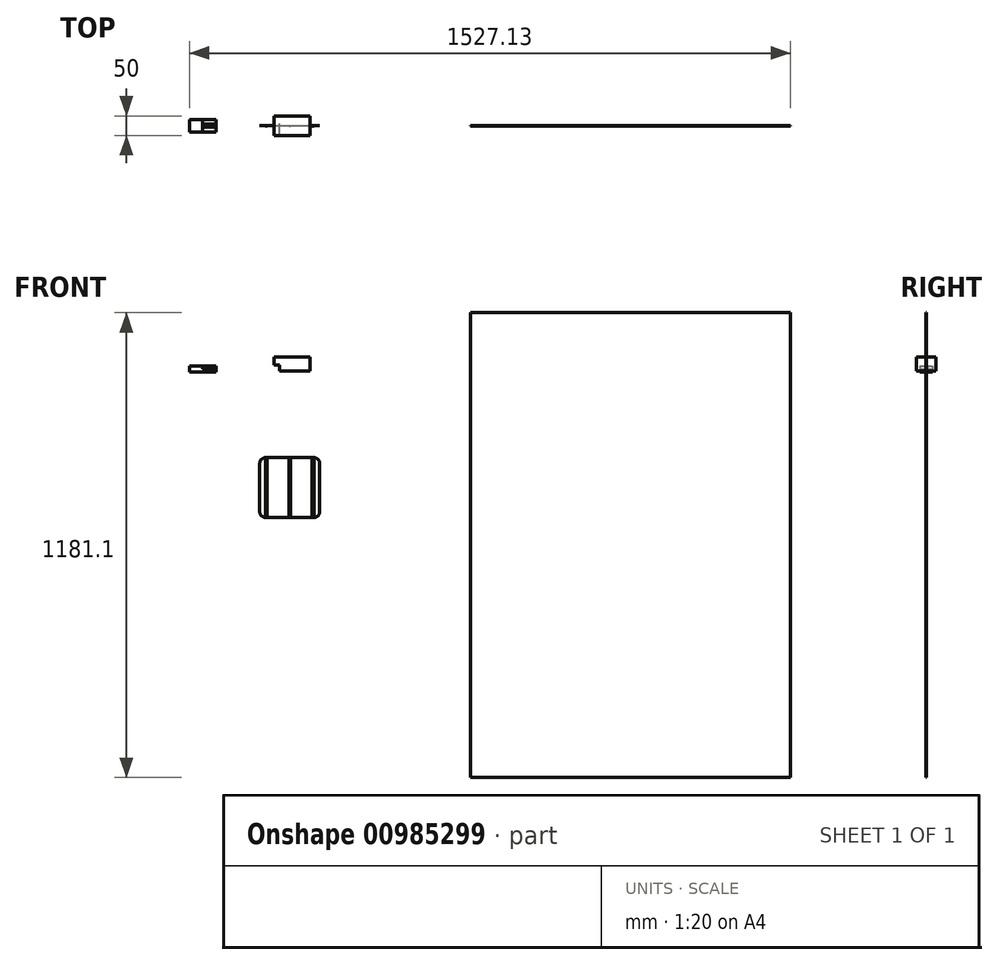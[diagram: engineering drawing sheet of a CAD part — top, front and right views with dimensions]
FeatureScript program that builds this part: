
annotation { "Feature Type Name" : "Feature", "Feature Type Description" : "" }
export const myFeature = defineFeature(function(context is Context, id is Id, definition is map)
    precondition{}
    {
        {
            var Q0;
            Q0=qCreatedBy(makeId("Front.planeOp"),FACE);
            var sketch = newSketch(context, id + "F0", { "sketchPlane" : qUnion([Q0])});
            skLineSegment(sketch, "E0", {"start": v(1286.74, 1046.2) * mm, "end": v(2099.54, 1046.2) * mm});
            skLineSegment(sketch, "E1", {"start": v(2099.54, -134.9) * mm, "end": v(1286.74, -134.9) * mm});
            skLineSegment(sketch, "E2", {"start": v(1286.74, 1046.2) * mm, "end": v(1286.74, -134.9) * mm});
            skLineSegment(sketch, "E3", {"start": v(2099.54, 1046.2) * mm, "end": v(2099.54, -134.9) * mm});
            skSolve(sketch);
        }
        {
            var Q0;
            Q0=makeQuery(id+"F0.imprint","IMPRINT",FACE,{"disambiguationData":[TD([[makeQuery(id+"F0.imprint","IMPRINT",EDGE,{"derivedFrom":sQuery(id+"F0.wireOp",EDGE,"E0")}),-1.0]])]});
            var sketch = newSketch(context, id + "F1", { "sketchPlane" : qUnion([Q0])});
            skLineSegment(sketch, "E4.bottom", {"start": v(766.3, 678.17) * mm, "end": v(888.7, 678.17) * mm});
            skLineSegment(sketch, "E4.top", {"start": v(766.3, 525.77) * mm, "end": v(888.7, 525.77) * mm});
            skLineSegment(sketch, "E4.left", {"start": v(751.3, 663.17) * mm, "end": v(751.3, 540.77) * mm});
            skLineSegment(sketch, "E4.right", {"start": v(903.7, 663.17) * mm, "end": v(903.7, 540.77) * mm});
            skPoint(sketch, "E5.visualSharp", {"position": v(751.3, 678.17) * mm});
            skArc(sketch, "E5.filletArc", {"start": v(766.3, 678.17) * mm, "mid": v(755.7, 673.78) * mm, "end": v(751.3, 663.17) * mm});
            skPoint(sketch, "E6.visualSharp", {"position": v(903.7, 678.17) * mm});
            skArc(sketch, "E6.filletArc", {"start": v(903.7, 663.17) * mm, "mid": v(899.3, 673.78) * mm, "end": v(888.7, 678.17) * mm});
            skPoint(sketch, "E7.visualSharp", {"position": v(903.7, 525.77) * mm});
            skArc(sketch, "E7.filletArc", {"start": v(888.7, 525.77) * mm, "mid": v(899.3, 530.16) * mm, "end": v(903.7, 540.77) * mm});
            skPoint(sketch, "E8.visualSharp", {"position": v(751.3, 525.77) * mm});
            skArc(sketch, "E8.filletArc", {"start": v(751.3, 540.77) * mm, "mid": v(755.7, 530.16) * mm, "end": v(766.3, 525.77) * mm});
            skLineSegment(sketch, "E9.bottom", {"start": v(3038.85, 81858.35) * mm, "end": v(2869.38, 81858.35) * mm});
            skLineSegment(sketch, "E9.top", {"start": v(3038.85, 72650.5) * mm, "end": v(2869.38, 72650.5) * mm});
            skLineSegment(sketch, "E9.left", {"start": v(3038.85, 81858.35) * mm, "end": v(3038.85, 72650.5) * mm});
            skLineSegment(sketch, "E9.right", {"start": v(2869.38, 81858.35) * mm, "end": v(2869.38, 72650.5) * mm});
            skSolve(sketch);
        }
        {
            var Q0;
            Q0=makeQuery(id+"F0.imprint","IMPRINT",FACE,{"disambiguationData":[TD([[makeQuery(id+"F0.imprint","IMPRINT",EDGE,{"derivedFrom":sQuery(id+"F0.wireOp",EDGE,"E0")}),-1.0]])]});
            extrude(context, id + "F2", {"entities" : qUnion([Q0]), "depth" : 1 * mm, "offsetDistance" : 25 * mm});
        }
        {
            var Q0;
            Q0=makeQuery(id+"F1.imprint","IMPRINT",FACE,{"disambiguationData":[TD([[makeQuery(id+"F1.imprint","IMPRINT",EDGE,{"derivedFrom":sQuery(id+"F1.wireOp",EDGE,"E4.bottom")}),-1.0]])]});
            extrude(context, id + "F3", {"entities" : qUnion([Q0]), "depth" : 1 * mm, "offsetDistance" : 25 * mm});
        }
        {
            var Q0;
            Q0=makeQuery(id+"F3.opExtrude","CAP_FACE",FACE,{"disambiguationData":[OSD([sQuery(id+"F1.wireOp",EDGE,"E4.bottom"),sQuery(id+"F1.wireOp",EDGE,"E4.top"),sQuery(id+"F1.wireOp",EDGE,"E4.left"),sQuery(id+"F1.wireOp",EDGE,"E4.right"),sQuery(id+"F1.wireOp",EDGE,"E5.filletArc"),sQuery(id+"F1.wireOp",EDGE,"E6.filletArc"),sQuery(id+"F1.wireOp",EDGE,"E7.filletArc"),sQuery(id+"F1.wireOp",EDGE,"E8.filletArc")])],"isStart":false});
            var sketch = newSketch(context, id + "F4", { "sketchPlane" : qUnion([Q0])});
            skLineSegment(sketch, "E10.bottom", {"start": v(1067.58, 689.47) * mm, "end": v(1071.78, 689.47) * mm});
            skLineSegment(sketch, "E10.top", {"start": v(1067.58, 537.07) * mm, "end": v(1071.78, 537.07) * mm});
            skLineSegment(sketch, "E10.left", {"start": v(1067.58, 689.47) * mm, "end": v(1067.58, 537.07) * mm});
            skLineSegment(sketch, "E10.right", {"start": v(1071.78, 689.47) * mm, "end": v(1071.78, 537.07) * mm});
            skLineSegment(sketch, "E11.bottom", {"start": v(1040.2, 697.09) * mm, "end": v(1044.38, 697.09) * mm});
            skLineSegment(sketch, "E11.top", {"start": v(1040.2, 544.69) * mm, "end": v(1044.38, 544.69) * mm});
            skLineSegment(sketch, "E11.left", {"start": v(1040.2, 697.09) * mm, "end": v(1040.2, 544.69) * mm});
            skLineSegment(sketch, "E11.right", {"start": v(1044.38, 697.09) * mm, "end": v(1044.38, 544.69) * mm});
            skLineSegment(sketch, "E12.bottom", {"start": v(998.8, 676.8) * mm, "end": v(1003, 676.8) * mm});
            skLineSegment(sketch, "E12.top", {"start": v(998.8, 524.4) * mm, "end": v(1003, 524.4) * mm});
            skLineSegment(sketch, "E12.left", {"start": v(998.8, 676.8) * mm, "end": v(998.8, 524.4) * mm});
            skLineSegment(sketch, "E12.right", {"start": v(1003, 676.8) * mm, "end": v(1003, 524.4) * mm});
            skSolve(sketch);
        }
        {
            var Q0;
            Q0=makeQuery(id+"F4.imprint","IMPRINT",FACE,{"disambiguationData":[TD([[makeQuery(id+"F4.imprint","IMPRINT",EDGE,{"derivedFrom":sQuery(id+"F4.wireOp",EDGE,"E10.bottom")}),-1.0]])]});
            var Q1;
            Q1=makeQuery(id+"F4.imprint","IMPRINT",FACE,{"disambiguationData":[TD([[makeQuery(id+"F4.imprint","IMPRINT",EDGE,{"derivedFrom":sQuery(id+"F4.wireOp",EDGE,"E11.bottom")}),-1.0]])]});
            var Q2;
            Q2=makeQuery(id+"F4.imprint","IMPRINT",FACE,{"disambiguationData":[TD([[makeQuery(id+"F4.imprint","IMPRINT",EDGE,{"derivedFrom":sQuery(id+"F4.wireOp",EDGE,"E12.bottom")}),-1.0]])]});
            extrude(context, id + "F5", {"entities" : qUnion([Q0, Q1, Q2]), "depth" : 0.5 * mm, "offsetDistance" : 25 * mm});
        }
        {
            var Q0;
            Q0=makeQuery(id+"F5.opExtrude","SWEPT_BODY",BODY,{"disambiguationData":[OSD([sQuery(id+"F4.wireOp",EDGE,"E12.bottom"),sQuery(id+"F4.wireOp",EDGE,"E12.top"),sQuery(id+"F4.wireOp",EDGE,"E12.left"),sQuery(id+"F4.wireOp",EDGE,"E12.right")])]});
            transform(context, id + "F6", {"entities" : qUnion([Q0]), "transformType" : TransformType.TRANSLATION_3D, "dx" : -232.8 * mm, "dy" : 0 * mm, "dz" : 3.3 * mm, "makeCopy" : false});
        }
        {
            var Q0;
            Q0=makeQuery(id+"F5.opExtrude","SWEPT_BODY",BODY,{"disambiguationData":[OSD([sQuery(id+"F4.wireOp",EDGE,"E12.bottom"),sQuery(id+"F4.wireOp",EDGE,"E12.top"),sQuery(id+"F4.wireOp",EDGE,"E12.left"),sQuery(id+"F4.wireOp",EDGE,"E12.right")])]});
            transform(context, id + "F7", {"entities" : qUnion([Q0]), "transformType" : TransformType.TRANSLATION_3D, "dx" : 6E-4000 * mm, "dy" : 0 * mm, "dz" : 0 * mm, "makeCopy" : false});
        }
        {
            var Q0;
            Q0=makeQuery(id+"F5.opExtrude","SWEPT_BODY",BODY,{"disambiguationData":[OSD([sQuery(id+"F4.wireOp",EDGE,"E12.bottom"),sQuery(id+"F4.wireOp",EDGE,"E12.top"),sQuery(id+"F4.wireOp",EDGE,"E12.left"),sQuery(id+"F4.wireOp",EDGE,"E12.right")])]});
            var Q1;
            Q1=makeQuery(id+"F5.opExtrude","CAP_VERTEX",VERTEX,{"disambiguationData":[OSD([sQuery(id+"F4.wireOp",EDGE,"E12.top"),sQuery(id+"F4.wireOp",EDGE,"E12.left")])],"isStart":false});
            var Q2;
            Q2=makeQuery(id+"F3.opExtrude","CAP_EDGE",EDGE,{"disambiguationData":[OSD([sQuery(id+"F1.wireOp",EDGE,"E4.top")])],"isStart":false});
            transform(context, id + "F8", {"entities" : qUnion([Q0]), "transformType" : TransformType.TRANSLATION_ENTITY, "oppositeDirectionEntity" : false, "transformLine" : qUnion([Q1, Q2]), "makeCopy" : false});
        }
        {
            var Q0;
            Q0=makeQuery(id+"F5.opExtrude","SWEPT_BODY",BODY,{"disambiguationData":[OSD([sQuery(id+"F4.wireOp",EDGE,"E12.bottom"),sQuery(id+"F4.wireOp",EDGE,"E12.top"),sQuery(id+"F4.wireOp",EDGE,"E12.left"),sQuery(id+"F4.wireOp",EDGE,"E12.right")])]});
            var Q1;
            Q1=makeQuery(id+"F5.opExtrude","CAP_VERTEX",VERTEX,{"disambiguationData":[OSD([sQuery(id+"F4.wireOp",EDGE,"E12.bottom"),sQuery(id+"F4.wireOp",EDGE,"E12.right")])],"isStart":true});
            var Q2;
            Q2=makeQuery(id+"F3.opExtrude","CAP_VERTEX",VERTEX,{"disambiguationData":[OSD([sQuery(id+"F1.wireOp",EDGE,"E4.bottom"),sQuery(id+"F1.wireOp",EDGE,"E6.filletArc")])],"isStart":false});
            transform(context, id + "F9", {"entities" : qUnion([Q0]), "transformType" : TransformType.TRANSLATION_ENTITY, "oppositeDirectionEntity" : false, "transformLine" : qUnion([Q1, Q2]), "makeCopy" : false});
        }
        {
            var Q0;
            Q0=makeQuery(id+"F5.opExtrude","SWEPT_BODY",BODY,{"disambiguationData":[OSD([sQuery(id+"F4.wireOp",EDGE,"E11.bottom"),sQuery(id+"F4.wireOp",EDGE,"E11.top"),sQuery(id+"F4.wireOp",EDGE,"E11.left"),sQuery(id+"F4.wireOp",EDGE,"E11.right")])]});
            var Q1;
            Q1=sQuery(id+"F4.wireOp",VERTEX,"E11.bottom.start");
            var Q2;
            Q2=makeQuery(id+"F3.opExtrude","CAP_VERTEX",VERTEX,{"disambiguationData":[OSD([sQuery(id+"F1.wireOp",EDGE,"E4.bottom"),sQuery(id+"F1.wireOp",EDGE,"E5.filletArc")])],"isStart":false});
            transform(context, id + "F10", {"entities" : qUnion([Q0]), "transformType" : TransformType.TRANSLATION_ENTITY, "oppositeDirectionEntity" : false, "transformLine" : qUnion([Q1, Q2]), "makeCopy" : false});
        }
        {
            var Q0;
            Q0=sQuery(id+"F4.wireOp",EDGE,"E10.bottom");
            cPoint(context, id + "F11", {"entities" : qUnion([Q0]), "parameter" : 0.5});
        }
        {
            var Q0;
            Q0=makeQuery(id+"F3.opExtrude","CAP_EDGE",EDGE,{"disambiguationData":[OSD([sQuery(id+"F1.wireOp",EDGE,"E4.bottom")])],"isStart":false});
            cPoint(context, id + "F12", {"entities" : qUnion([Q0]), "parameter" : 0.5});
        }
        {
            var Q0;
            Q0=makeQuery(id+"F5.opExtrude","SWEPT_BODY",BODY,{"disambiguationData":[OSD([sQuery(id+"F4.wireOp",EDGE,"E10.bottom"),sQuery(id+"F4.wireOp",EDGE,"E10.top"),sQuery(id+"F4.wireOp",EDGE,"E10.left"),sQuery(id+"F4.wireOp",EDGE,"E10.right")])]});
            var Q1;
            Q1=qCreatedBy(id+"F11",VERTEX);
            var Q2;
            Q2=qCreatedBy(id+"F12",VERTEX);
            transform(context, id + "F13", {"entities" : qUnion([Q0]), "transformType" : TransformType.TRANSLATION_ENTITY, "oppositeDirectionEntity" : false, "transformLine" : qUnion([Q1, Q2]), "makeCopy" : false});
        }
        {
            var Q0;
            Q0=makeQuery(id+"F2.opExtrude","CAP_FACE",FACE,{"disambiguationData":[OSD([sQuery(id+"F0.wireOp",EDGE,"E0"),sQuery(id+"F0.wireOp",EDGE,"E1"),sQuery(id+"F0.wireOp",EDGE,"E2"),sQuery(id+"F0.wireOp",EDGE,"E3")])],"isStart":false});
            var sketch = newSketch(context, id + "F14", { "sketchPlane" : qUnion([Q0])});
            skLineSegment(sketch, "E13.bottom", {"start": v(801.5, 913.01) * mm, "end": v(878.96, 913.01) * mm});
            skLineSegment(sketch, "E13.top", {"start": v(801.5, 898.01) * mm, "end": v(878.96, 898.01) * mm});
            skLineSegment(sketch, "E13.left", {"start": v(801.5, 913.01) * mm, "end": v(801.5, 898.01) * mm});
            skLineSegment(sketch, "E13.right", {"start": v(878.96, 913.01) * mm, "end": v(878.96, 898.01) * mm});
            skLineSegment(sketch, "E14.bottom", {"start": v(878.96, 913.01) * mm, "end": v(787.59, 913.01) * mm});
            skLineSegment(sketch, "E14.top", {"start": v(878.96, 934.06) * mm, "end": v(787.59, 934.06) * mm});
            skLineSegment(sketch, "E14.left", {"start": v(878.96, 913.01) * mm, "end": v(878.96, 934.06) * mm});
            skLineSegment(sketch, "E14.right", {"start": v(787.59, 913.01) * mm, "end": v(787.59, 934.06) * mm});
            skLineSegment(sketch, "E15.bottom", {"start": v(787.59, 926.24) * mm, "end": v(765.52, 926.24) * mm});
            skLineSegment(sketch, "E15.top", {"start": v(787.59, 912.98) * mm, "end": v(765.52, 912.98) * mm});
            skLineSegment(sketch, "E15.left", {"start": v(787.59, 923.54) * mm, "end": v(787.59, 912.98) * mm});
            skLineSegment(sketch, "E15.right", {"start": v(765.52, 926.24) * mm, "end": v(765.52, 912.98) * mm});
            skSolve(sketch);
        }
        {
            var Q0;
            {var subQ1=sQuery(id+"F14.wireOp",EDGE,"E14.top");Q0=makeQuery(id+"F14.imprint","IMPRINT",FACE,{"disambiguationData":[TD([[makeQuery(id+"F14.imprint","IMPRINT",EDGE,{"derivedFrom":subQ1}),1.0]])]});}
            var sketch = newSketch(context, id + "F15", { "sketchPlane" : qUnion([Q0])});
            skLineSegment(sketch, "E16.bottom", {"start": v(-15.18, -3.1) * mm, "end": v(62.27, -3.1) * mm});
            skLineSegment(sketch, "E16.top", {"start": v(-15.18, -18.1) * mm, "end": v(62.27, -18.1) * mm});
            skLineSegment(sketch, "E16.left", {"start": v(-15.18, -3.1) * mm, "end": v(-15.18, -18.1) * mm});
            skLineSegment(sketch, "E16.right", {"start": v(62.27, -3.1) * mm, "end": v(62.27, -18.1) * mm});
            skLineSegment(sketch, "E17.bottom", {"start": v(62.27, -3.1) * mm, "end": v(-29.1, -3.1) * mm});
            skLineSegment(sketch, "E17.top", {"start": v(62.27, 17.96) * mm, "end": v(-29.1, 17.96) * mm});
            skLineSegment(sketch, "E17.left", {"start": v(62.27, -3.1) * mm, "end": v(62.27, 17.96) * mm});
            skLineSegment(sketch, "E17.right", {"start": v(-29.1, -3.1) * mm, "end": v(-29.1, 17.96) * mm});
            skLineSegment(sketch, "E18.bottom", {"start": v(-29.1, 10.13) * mm, "end": v(-51.17, 10.13) * mm});
            skLineSegment(sketch, "E18.top", {"start": v(-29.1, -3.13) * mm, "end": v(-51.17, -3.13) * mm});
            skLineSegment(sketch, "E18.left", {"start": v(-29.1, 7.43) * mm, "end": v(-29.1, -3.13) * mm});
            skLineSegment(sketch, "E18.right", {"start": v(-51.17, 10.13) * mm, "end": v(-51.17, -3.13) * mm});
            skLineSegment(sketch, "E19.top", {"start": v(572.41, 895.67) * mm, "end": v(640.41, 895.67) * mm});
            skLineSegment(sketch, "E19.left", {"start": v(572.41, 910.17) * mm, "end": v(572.41, 895.67) * mm});
            skLineSegment(sketch, "E20.bottom", {"start": v(572.41, 910.17) * mm, "end": v(606.41, 910.17) * mm});
            skLineSegment(sketch, "E20.top", {"start": v(572.41, 895.67) * mm, "end": v(606.41, 895.67) * mm});
            skLineSegment(sketch, "E20.right", {"start": v(606.41, 910.17) * mm, "end": v(606.41, 895.67) * mm});
            skLineSegment(sketch, "E21", {"start": v(606.41, 902.92) * mm, "end": v(640.41, 902.92) * mm});
            skLineSegment(sketch, "E22.top", {"start": v(606.41, 906.59) * mm, "end": v(640.41, 906.59) * mm});
            skLineSegment(sketch, "E22.left", {"start": v(606.41, 902.92) * mm, "end": v(606.41, 906.59) * mm});
            skLineSegment(sketch, "E22.right", {"start": v(640.41, 902.92) * mm, "end": v(640.41, 906.59) * mm});
            skLineSegment(sketch, "E23", {"start": v(640.41, 902.92) * mm, "end": v(640.41, 895.67) * mm});
            skSolve(sketch);
        }
        {
            var Q0;
            {var subQ3=sQuery(id+"F15.wireOp",EDGE,"fItkzUZf-nGmU-rPvr-P6rd-NpfCkkb8rq9y.bottom");Q0=makeQuery(id+"F15.imprint","IMPRINT",FACE,{"disambiguationData":[TD([[makeQuery(id+"F15.imprint","IMPRINT",EDGE,{"derivedFrom":subQ3}),-1.0]])]});}
            var Q1;
            Q1=makeQuery(id+"F15.imprint","IMPRINT",FACE,{"disambiguationData":[TD([[makeQuery(id+"F15.imprint","IMPRINT",EDGE,{"derivedFrom":sQuery(id+"F15.wireOp",EDGE,"4efb6f42-2137-4167-9bb1-179bed798946.left")}),-1.0]])]});
            var Q2;
            {var subQ1=sQuery(id+"F14.wireOp",EDGE,"E14.top");Q2=makeQuery(id+"F14.imprint","IMPRINT",FACE,{"disambiguationData":[TD([[makeQuery(id+"F14.imprint","IMPRINT",EDGE,{"derivedFrom":subQ1}),1.0]])]});}
            var Q3;
            Q3=makeQuery(id+"F14.imprint","IMPRINT",FACE,{"disambiguationData":[TD([[makeQuery(id+"F14.imprint","IMPRINT",EDGE,{"derivedFrom":sQuery(id+"F14.wireOp",EDGE,"E13.top")}),1.0]])]});
            extrude(context, id + "F16", {"entities" : qUnion([Q0, Q1, Q2, Q3]), "endBound" : BoundingType.SYMMETRIC, "depth" : 50 * mm, "offsetDistance" : 25 * mm});
        }
        {
            var Q0;
            {var subQ1=sQuery(id+"F15.wireOp",EDGE,"E20.bottom");Q0=makeQuery(id+"F15.imprint","IMPRINT",FACE,{"disambiguationData":[TD([[makeQuery(id+"F15.imprint","IMPRINT",EDGE,{"derivedFrom":subQ1}),-1.0]])]});}
            var Q1;
            {var subQ0=sQuery(id+"F15.wireOp",EDGE,"E19.top");Q1=makeQuery(id+"F15.imprint","IMPRINT",FACE,{"disambiguationData":[TD([[makeQuery(id+"F15.imprint","IMPRINT",EDGE,{"derivedFrom":subQ0}),1.0]])]});}
            extrude(context, id + "F17", {"entities" : qUnion([Q0, Q1]), "endBound" : BoundingType.SYMMETRIC, "depth" : 31 * mm, "offsetDistance" : 25 * mm});
        }
        {
            var Q0;
            Q0=makeQuery(id+"F15.imprint","IMPRINT",FACE,{"disambiguationData":[TD([[makeQuery(id+"F15.imprint","IMPRINT",EDGE,{"derivedFrom":sQuery(id+"F15.wireOp",EDGE,"E21")}),1.0]])]});
            var Q1;
            Q1=sQuery(id+"F15.wireOp",EDGE,"E22.top");
            revolve(context, id + "F18", {"surfaceOperationType" : NewSurfaceOperationType.NEW, "entities" : qUnion([Q0]), "axis" : qUnion([Q1]), "revolveType" : RevolveType.FULL});
        }
        {
            var Q0;
            Q0=makeQuery(id+"F14.imprint","IMPRINT",FACE,{"disambiguationData":[TD([[makeQuery(id+"F14.imprint","IMPRINT",EDGE,{"derivedFrom":makeQuery(id+"F2.opExtrude","CAP_EDGE",EDGE,{"disambiguationData":[OSD([sQuery(id+"F0.wireOp",EDGE,"E0")])],"isStart":false})}),-1.0]])]});
            extrude(context, id + "F19", {"entities" : qUnion([Q0]), "depth" : 1 * mm, "offsetDistance" : 25.4 * mm});
        }
    });
